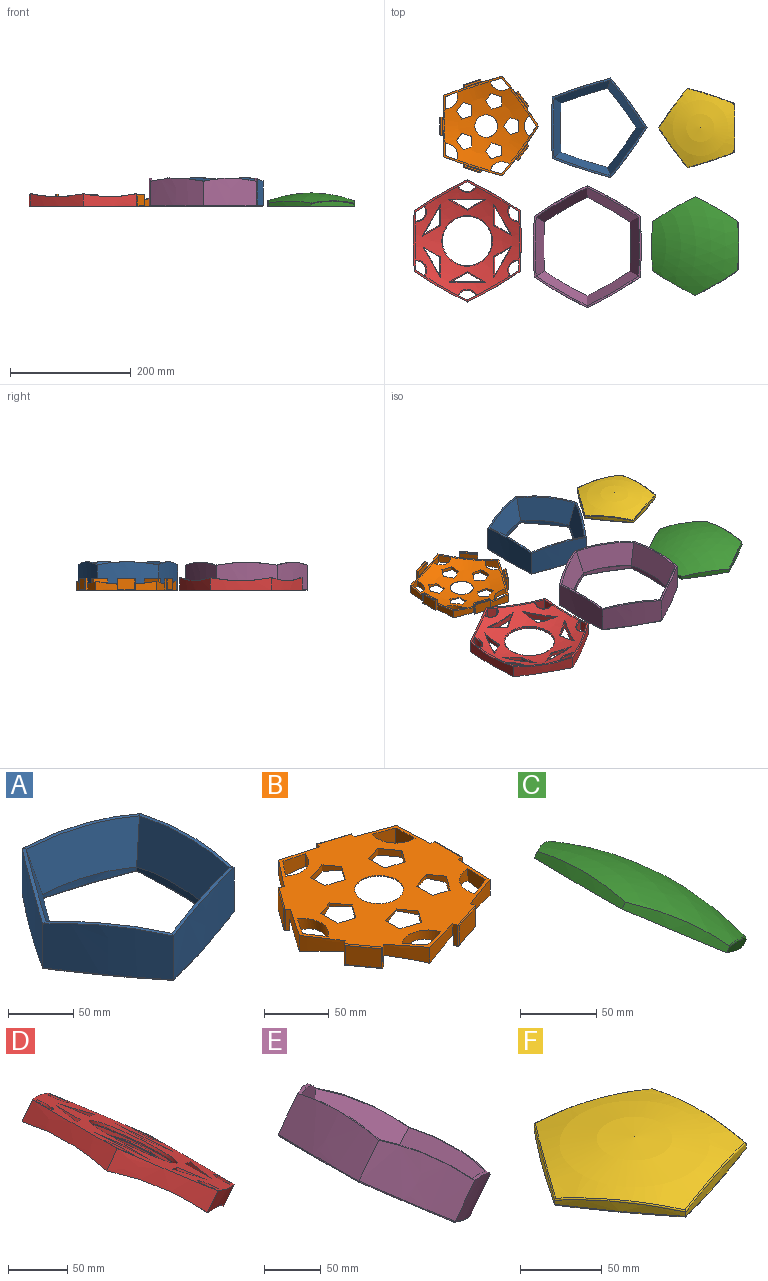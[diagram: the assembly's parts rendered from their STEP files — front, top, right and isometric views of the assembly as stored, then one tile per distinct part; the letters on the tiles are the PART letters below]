
ASSEMBLY  parts=6 mates=5
PART A: 31 faces, bbox 185.7x195.3x47.6 mm
  f0: plane 92.99x43.22mm, normal (-0.3,-0.91,0.28), area 3660.3mm2, adj f1,f2,f9,f15
  f1: plane 97.76x43.22mm, normal (-0.96,0,0.28), area 3660.3mm2, adj f0,f3,f5,f11
  f2: plane 79.14x61.88mm, normal (0.78,-0.56,0.28), area 3660.3mm2, adj f0,f4,f8,f14
  f3: plane 92.99x43.22mm, normal (-0.3,0.91,0.28), area 3660.3mm2, adj f1,f4,f6,f12
  f4: plane 79.14x61.88mm, normal (0.78,0.56,0.28), area 3660.3mm2, adj f2,f3,f7,f13
  f5: extruded ~81.11x7.29mm, area 485.1mm2, adj f1,f6,f9,f28
  f6: extruded ~77.14x25.06mm, area 485.1mm2, adj f3,f5,f7,f26
  f7: extruded ~65.62x47.67mm, area 485.1mm2, adj f4,f6,f8,f27
  f8: extruded ~65.62x47.67mm, area 485.1mm2, adj f2,f7,f9,f29
  f9: extruded ~77.14x25.06mm, area 485.1mm2, adj f0,f5,f8,f30
  f10: plane 162.33x155.86mm, normal (0,0,-1), area 5769.7mm2, adj f21,f22,f23,f24,f25,f26,f27,f28
  f11: bspline ~101.71x5.13mm, area 300.7mm2, adj f1,f12,f15,f18
  f12: bspline ~97.49x34.22mm, area 300.7mm2, adj f3,f11,f13,f19
  f13: bspline ~83.9x62.1mm, area 300.7mm2, adj f4,f12,f14,f20
  f14: bspline ~83.9x62.1mm, area 300.7mm2, adj f2,f13,f15,f16
  f15: bspline ~97.49x34.22mm, area 300.7mm2, adj f0,f11,f14,f17
  f16: extruded ~82.29x59.79mm, area 4192.3mm2, adj f14,f17,f20,f25
  f17: extruded ~96.73x41.19mm, area 4192.3mm2, adj f15,f16,f18,f23
  f18: extruded ~101.71x41.19mm, area 4192.3mm2, adj f11,f17,f19,f21
  f19: extruded ~96.73x41.19mm, area 4192.3mm2, adj f12,f18,f20,f22
  f20: extruded ~82.29x59.79mm, area 4192.3mm2, adj f13,f16,f19,f24
  f21: bspline ~141.48x3.96mm, area 158.8mm2, adj f10,f18,f22,f23
  f22: bspline ~134.78x44.64mm, area 158.8mm2, adj f10,f19,f21,f24
  f23: bspline ~134.78x44.64mm, area 158.8mm2, adj f10,f17,f21,f25
  f24: bspline ~114.98x83.92mm, area 158.8mm2, adj f10,f20,f22,f25
  f25: bspline ~114.98x83.92mm, area 158.8mm2, adj f10,f16,f23,f24
  f26: bspline ~109.03x36.27mm, area 128.5mm2, adj f6,f10,f27,f28
  f27: bspline ~93.07x68mm, area 128.5mm2, adj f7,f10,f26,f29
  f28: bspline ~114.4x3.32mm, area 128.5mm2, adj f5,f10,f26,f30
  f29: bspline ~93.07x68mm, area 128.5mm2, adj f8,f10,f27,f30
  f30: bspline ~109.03x36.27mm, area 128.5mm2, adj f9,f10,f28,f29
PART B: 113 faces, bbox 165.4x167x22.5 mm
  f0: extruded ~50.72x15.01mm, area 441.3mm2, adj f19,f43,f52,f103,f111
  f1: extruded ~48.71x15.01mm, area 441.3mm2, adj f19,f46,f51,f92,f100
  f2: extruded ~41.93x28.58mm, area 441.3mm2, adj f19,f45,f50,f81,f89
  f3: extruded ~40.14x31.04mm, area 441.3mm2, adj f19,f47,f56,f70,f78
  f4: extruded ~47.77x17.12mm, area 441.3mm2, adj f19,f44,f57,f59,f67
  f5: sphere r=242.5mm, area 11570.5mm2, adj f6,f7,f8,f9,f10,f11,f12,f13
  f6: cylinder r=20mm len=31.77mm, axis (0,0,1), area 372.4mm2, adj f5,f19,f40,f53
  f7: cylinder r=20mm len=33.41mm, axis (0,0,1), area 372.4mm2, adj f5,f19,f38,f55
  f8: cylinder r=20mm len=31.77mm, axis (0,0,1), area 372.4mm2, adj f5,f19,f39,f54
  f9: plane 16.51x7.46mm, normal (1,0,0), area 74.6mm2, adj f5,f10,f19,f35
  f10: plane 19.6x7.94mm, normal (0.31,-0.95,0), area 115.8mm2, adj f5,f9,f19,f36
  f11: plane 15.76x7.46mm, normal (0.31,0.95,0), area 74.6mm2, adj f5,f12,f19,f32
  f12: plane 20.52x7.94mm, normal (1,0,0), area 115.8mm2, adj f5,f11,f19,f33
  f13: plane 13.58x10.19mm, normal (-0.81,0.59,0), area 74.6mm2, adj f5,f14,f19,f29
  f14: plane 19.6x7.94mm, normal (0.31,0.95,0), area 115.8mm2, adj f5,f13,f19,f30
  f15: plane 12.88x9.49mm, normal (-0.81,-0.59,0), area 74.6mm2, adj f5,f16,f19,f26
  f16: plane 16.92x12.75mm, normal (-0.81,0.59,0), area 115.8mm2, adj f5,f15,f19,f27
  f17: plane 15.76x7.46mm, normal (0.31,-0.95,0), area 74.6mm2, adj f5,f18,f19,f23
  f18: plane 16.92x12.75mm, normal (-0.81,-0.59,0), area 115.8mm2, adj f5,f17,f19,f24
  f19: plane 164.57x161.91mm, normal (0,0,1), area 13363.7mm2, adj f0,f1,f2,f3,f4,f6,f7,f8
  f20: cylinder r=20mm len=27.05mm, axis (0,0,1), area 372.4mm2, adj f5,f19,f41,f48
  f21: cylinder r=20mm len=27.05mm, axis (0,0,1), area 372.4mm2, adj f5,f19,f42,f49
  f22: cylinder r=18.8mm len=37.59mm, axis (0,0,1), area 86.1mm2, adj f5,f19
  f23: plane 19.95x6.1mm, normal (1,0,0), area 45.3mm2, adj f5,f17,f19,f25
  f24: plane 13.58x10.19mm, normal (-0.81,0.59,0), area 74.6mm2, adj f5,f18,f19,f25
  f25: plane 19.1x7.86mm, normal (0.31,0.95,0), area 45.3mm2, adj f5,f19,f23,f24
  f26: plane 17.53x6.3mm, normal (0.31,-0.95,0), area 45.3mm2, adj f5,f15,f19,f28
  f27: plane 15.76x7.46mm, normal (0.31,0.95,0), area 74.6mm2, adj f5,f16,f19,f28
  f28: plane 19.95x6.1mm, normal (1,0,0), area 45.3mm2, adj f5,f19,f26,f27
  f29: plane 16.61x12.74mm, normal (-0.81,-0.59,0), area 45.3mm2, adj f5,f13,f19,f31
  f30: plane 16.51x7.46mm, normal (1,0,0), area 74.6mm2, adj f5,f14,f19,f31
  f31: plane 19.1x7.86mm, normal (0.31,-0.95,0), area 45.3mm2, adj f5,f19,f29,f30
  f32: plane 16.61x12.74mm, normal (-0.81,0.59,0), area 45.3mm2, adj f5,f11,f19,f34
  f33: plane 15.76x7.46mm, normal (0.31,-0.95,0), area 74.6mm2, adj f5,f12,f19,f34
  f34: plane 16.61x12.74mm, normal (-0.81,-0.59,0), area 45.3mm2, adj f5,f19,f32,f33
  f35: plane 19.1x7.86mm, normal (0.31,0.95,0), area 45.3mm2, adj f5,f9,f19,f37
  f36: plane 13.58x10.19mm, normal (-0.81,-0.59,0), area 74.6mm2, adj f5,f10,f19,f37
  f37: plane 16.61x12.74mm, normal (-0.81,0.59,0), area 45.3mm2, adj f5,f19,f35,f36
  f38: extruded ~16.7x14.63mm, area 261.5mm2, adj f7,f19,f47,f55
  f39: extruded ~15.62x14.63mm, area 261.5mm2, adj f8,f19,f45,f54
  f40: extruded ~19.29x14.63mm, area 261.5mm2, adj f6,f19,f44,f53
  f41: extruded ~19.98x14.63mm, area 261.5mm2, adj f19,f20,f43,f48
  f42: extruded ~18.72x14.63mm, area 261.5mm2, adj f19,f21,f46,f49
  f43: bspline ~101.71x5.12mm, area 300.9mm2, adj f0,f5,f41,f44,f46,f49,f57,f111
  f44: bspline ~97.49x34.22mm, area 300.9mm2, adj f4,f5,f40,f43,f47,f48,f56,f67
  f45: bspline ~83.9x62.1mm, area 300.9mm2, adj f2,f5,f39,f46,f47,f51,f55,f89
  f46: bspline ~97.49x34.22mm, area 300.9mm2, adj f1,f5,f42,f43,f45,f52,f54,f100
  f47: bspline ~83.9x62.1mm, area 300.9mm2, adj f3,f5,f38,f44,f45,f50,f53,f78
  f48: extruded ~18.72x14.63mm, area 261.5mm2, adj f19,f20,f41,f44
  f49: extruded ~19.98x14.63mm, area 261.5mm2, adj f19,f21,f42,f43
  f50: extruded ~41.93x28.58mm, area 441.4mm2, adj f2,f19,f47,f69,f78
  f51: extruded ~40.14x31.05mm, area 441.4mm2, adj f1,f19,f45,f80,f89
  f52: extruded ~47.77x17.12mm, area 441.4mm2, adj f0,f19,f46,f91,f100
  f53: extruded ~15.62x14.63mm, area 261.5mm2, adj f6,f19,f40,f47
  f54: extruded ~19.29x14.63mm, area 261.5mm2, adj f8,f19,f39,f46
  f55: extruded ~16.7x14.63mm, area 261.5mm2, adj f7,f19,f38,f45
  f56: extruded ~48.71x15.01mm, area 441.4mm2, adj f3,f19,f44,f58,f67
  f57: extruded ~50.72x15.01mm, area 441.4mm2, adj f4,f19,f43,f102,f111
  f58: plane 20x3.8mm, normal (-0.95,0.31,0), area 75.7mm2, adj f19,f56,f60,f62,f66,f67,f68
  f59: plane 20x3.8mm, normal (0.95,-0.31,0), area 75.7mm2, adj f4,f19,f60,f65,f66,f67,f68
  f60: plane 29.34x11.74mm, normal (0,0,-1), area 78mm2, adj f58,f59,f63,f68
  f61: plane 26.63x18mm, normal (0.31,0.95,0), area 504mm2, adj f62,f63,f64,f65
  f62: cylinder r=1mm len=20mm, axis (0,0,-1), area 29.8mm2, adj f58,f61,f63,f64
  f63: cylinder r=1mm len=28.84mm, axis (0.95,-0.31,0), area 45.6mm2, adj f60,f61,f62,f65
  f64: cylinder r=1mm len=28.84mm, axis (-0.95,0.31,0), area 45.6mm2, adj f19,f61,f62,f65
  f65: cylinder r=1mm len=20mm, axis (0,0,1), area 29.8mm2, adj f59,f61,f63,f64
  f66: plane 28.53x9.27mm, normal (-0.31,-0.95,0), area 273.5mm2, adj f58,f59,f67,f68
  f67: plane 28.66x9.65mm, normal (0,0,-1), area 9.4mm2, adj f4,f44,f56,f58,f59,f66
  f68: cylinder r=1mm len=28.84mm, axis (0.95,-0.31,0), area 47.1mm2, adj f58,f59,f60,f66
  f69: plane 20x3.24mm, normal (-0.59,-0.81,0), area 75.7mm2, adj f19,f50,f71,f73,f77,f78,f79
  f70: plane 20x3.24mm, normal (0.59,0.81,0), area 75.7mm2, adj f3,f19,f71,f76,f77,f78,f79
  f71: plane 25.8x19.74mm, normal (0,0,-1), area 78mm2, adj f69,f70,f74,f79
  f72: plane 22.65x18mm, normal (-0.81,0.59,0), area 504mm2, adj f73,f74,f75,f76
  f73: cylinder r=1mm len=20mm, axis (0,0,-1), area 29.8mm2, adj f69,f72,f74,f75
  f74: cylinder r=1mm len=24.86mm, axis (0.59,0.81,0), area 45.6mm2, adj f71,f72,f73,f76
  f75: cylinder r=1mm len=24.86mm, axis (-0.59,-0.81,0), area 45.6mm2, adj f19,f72,f73,f76
  f76: cylinder r=1mm len=20mm, axis (0,0,1), area 29.8mm2, adj f70,f72,f74,f75
  f77: plane 24.27x17.63mm, normal (0.81,-0.59,0), area 273.5mm2, adj f69,f70,f78,f79
  f78: plane 24.51x17.96mm, normal (0,0,-1), area 9.4mm2, adj f3,f47,f50,f69,f70,f77
  f79: cylinder r=1mm len=24.86mm, axis (0.59,0.81,0), area 47.1mm2, adj f69,f70,f71,f77
  f80: plane 20x3.24mm, normal (0.59,-0.81,0), area 75.7mm2, adj f19,f51,f82,f84,f88,f89,f90
  f81: plane 20x3.24mm, normal (-0.59,0.81,0), area 75.7mm2, adj f2,f19,f82,f87,f88,f89,f90
  f82: plane 25.8x19.74mm, normal (0,0,-1), area 78mm2, adj f80,f81,f85,f90
  f83: plane 22.65x18mm, normal (-0.81,-0.59,0), area 504mm2, adj f84,f85,f86,f87
  f84: cylinder r=1mm len=20mm, axis (0,0,-1), area 29.8mm2, adj f80,f83,f85,f86
  f85: cylinder r=1mm len=24.86mm, axis (-0.59,0.81,0), area 45.6mm2, adj f82,f83,f84,f87
  f86: cylinder r=1mm len=24.86mm, axis (0.59,-0.81,0), area 45.6mm2, adj f19,f83,f84,f87
  f87: cylinder r=1mm len=20mm, axis (0,0,1), area 29.8mm2, adj f81,f83,f85,f86
  f88: plane 24.27x17.63mm, normal (0.81,0.59,0), area 273.5mm2, adj f80,f81,f89,f90
  f89: plane 24.51x17.96mm, normal (0,0,-1), area 9.4mm2, adj f2,f45,f51,f80,f81,f88
  f90: cylinder r=1mm len=24.86mm, axis (-0.59,0.81,0), area 47.1mm2, adj f80,f81,f82,f88
  f91: plane 20x3.8mm, normal (0.95,0.31,0), area 75.7mm2, adj f19,f52,f93,f95,f99,f100,f101
  f92: plane 20x3.8mm, normal (-0.95,-0.31,0), area 75.7mm2, adj f1,f19,f93,f98,f99,f100,f101
  f93: plane 29.34x11.74mm, normal (0,0,-1), area 78mm2, adj f91,f92,f96,f101
  f94: plane 26.63x18mm, normal (0.31,-0.95,0), area 504mm2, adj f95,f96,f97,f98
  f95: cylinder r=1mm len=20mm, axis (0,0,-1), area 29.8mm2, adj f91,f94,f96,f97
  f96: cylinder r=1mm len=28.84mm, axis (-0.95,-0.31,0), area 45.6mm2, adj f93,f94,f95,f98
  f97: cylinder r=1mm len=28.84mm, axis (0.95,0.31,0), area 45.6mm2, adj f19,f94,f95,f98
  f98: cylinder r=1mm len=20mm, axis (0,0,1), area 29.8mm2, adj f92,f94,f96,f97
  f99: plane 28.53x9.27mm, normal (-0.31,0.95,0), area 273.5mm2, adj f91,f92,f100,f101
  f100: plane 28.66x9.65mm, normal (0,0,-1), area 9.4mm2, adj f1,f46,f52,f91,f92,f99
  f101: cylinder r=1mm len=28.84mm, axis (-0.95,-0.31,0), area 47.1mm2, adj f91,f92,f93,f99
  f102: plane 20x4mm, normal (0,1,0), area 75.7mm2, adj f19,f57,f104,f106,f110,f111,f112
  f103: plane 20x4mm, normal (0,-1,0), area 75.7mm2, adj f0,f19,f104,f109,f110,f111,f112
  f104: plane 30x2.6mm, normal (0,0,-1), area 78mm2, adj f102,f103,f107,f112
  f105: plane 28x18mm, normal (1,0,0), area 504mm2, adj f106,f107,f108,f109
  f106: cylinder r=1mm len=20mm, axis (0,0,-1), area 29.8mm2, adj f102,f105,f107,f108
  f107: cylinder r=1mm len=30mm, axis (0,-1,0), area 45.6mm2, adj f104,f105,f106,f109
  f108: cylinder r=1mm len=30mm, axis (0,1,0), area 45.6mm2, adj f19,f105,f106,f109
  f109: cylinder r=1mm len=20mm, axis (0,0,1), area 29.8mm2, adj f103,f105,f107,f108
  f110: plane 30x9.12mm, normal (-1,0,0), area 273.5mm2, adj f102,f103,f111,f112
  f111: plane 30x0.4mm, normal (0,0,-1), area 9.4mm2, adj f0,f43,f57,f102,f103,f110
  f112: cylinder r=1mm len=30mm, axis (0,-1,0), area 47.1mm2, adj f102,f103,f104,f110
PART C: 27 faces, bbox 126.4x203x94.5 mm
  f0: plane 29.86x26.12mm, normal (0.4,0.87,-0.3), area 345.6mm2, adj f1,f2,f18,f26
  f1: cylinder r=15.23mm len=15.44mm, axis (-0.61,0,-0.79), area 161.9mm2, adj f0,f3,f18,f26
  f2: cylinder r=50mm len=50mm, axis (-0.61,0,-0.79), area 523.6mm2, adj f0,f3,f18,f26
  f3: plane 29.86x26.12mm, normal (0.4,-0.87,-0.3), area 345.6mm2, adj f1,f2,f18,f26
  f4: cylinder r=50mm len=40.48mm, axis (-0.61,0,-0.79), area 523.6mm2, adj f5,f6,f18,f25
  f5: plane 34.77x7.95mm, normal (-0.79,0,0.61), area 347.7mm2, adj f4,f7,f18,f25
  f6: plane 30.14x26.33mm, normal (0.4,-0.87,-0.3), area 349.7mm2, adj f4,f7,f18,f25
  f7: cylinder r=15.23mm len=16.41mm, axis (-0.61,0,-0.79), area 158.4mm2, adj f5,f6,f18,f25
  f8: plane 34.77x7.95mm, normal (-0.79,0,0.61), area 347.7mm2, adj f9,f10,f18,f24
  f9: cylinder r=15.23mm len=16.41mm, axis (-0.61,0,-0.79), area 158.4mm2, adj f8,f11,f18,f24
  f10: cylinder r=50mm len=40.48mm, axis (-0.61,0,-0.79), area 523.6mm2, adj f8,f11,f18,f24
  f11: plane 30.14x26.33mm, normal (0.4,0.87,-0.3), area 349.7mm2, adj f9,f10,f18,f24
  f12: cylinder r=10mm len=21.96mm, axis (-0.61,0,-0.79), area 628.3mm2, adj f18,f23
  f13: sphere r=202.5mm, area 18663.9mm2, adj f16,f17,f19,f20,f21,f22
  f14: extruded ~61.02x49.32mm, area 561.6mm2, adj f15,f17,f18,f21
  f15: extruded ~81.46x7.4mm, area 561.6mm2, adj f14,f16,f18,f22
  f16: extruded ~61.44x49.87mm, area 617.9mm2, adj f13,f15,f18,f19,f22
  f17: extruded ~61.44x49.87mm, area 617.9mm2, adj f13,f14,f18,f20,f21
  f18: plane 162.92x114.47mm, normal (-0.61,0,-0.79), area 13845.5mm2, adj f0,f1,f2,f3,f4,f5,f6,f7
  f19: extruded ~61.44x49.87mm, area 618.1mm2, adj f13,f16,f18,f20
  f20: extruded ~81.46x7.94mm, area 618.1mm2, adj f13,f17,f18,f19
  f21: bspline ~62.43x48.26mm, area 99.2mm2, adj f13,f14,f17,f22
  f22: bspline ~91.5x4.94mm, area 99.2mm2, adj f13,f15,f16,f21
  f23: plane 20x15.89mm, normal (-0.61,0,-0.79), area 314.2mm2, adj f12
  f24: plane 42.48x34.41mm, normal (-0.61,0,-0.79), area 1189.3mm2, adj f8,f9,f10,f11
  f25: plane 42.48x34.41mm, normal (-0.61,0,-0.79), area 1189.3mm2, adj f4,f5,f6,f7
  f26: plane 50x29.11mm, normal (-0.61,0,-0.79), area 1183.9mm2, adj f0,f1,f2,f3
PART D: 75 faces, bbox 163.4x243.7x126.1 mm
  f0: sphere r=242.5mm, area 16081.2mm2, adj f23,f33,f34,f35,f36,f37,f38,f51
  f1: cylinder r=16.14mm len=25.05mm, axis (0.61,0,0.79), area 598.9mm2, adj f6,f29,f42,f73
  f2: cylinder r=16.14mm len=25.05mm, axis (0.61,0,0.79), area 598.9mm2, adj f6,f28,f41,f72
  f3: cylinder r=16.14mm len=33.12mm, axis (0.61,0,0.79), area 598.9mm2, adj f6,f27,f40,f71
  f4: cylinder r=16.14mm len=25.05mm, axis (0.61,0,0.79), area 598.9mm2, adj f6,f30,f39,f70
  f5: cylinder r=16.14mm len=25.05mm, axis (0.61,0,0.79), area 598.9mm2, adj f6,f32,f44,f69
  f6: plane 201.9x141.94mm, normal (0.61,0,0.79), area 17762.9mm2, adj f1,f2,f3,f4,f5,f7,f8,f9
  f7: cylinder r=16.14mm len=33.12mm, axis (0.61,0,0.79), area 598.9mm2, adj f6,f31,f43,f51
  f8: plane 24.04x23.88mm, normal (-0.4,-0.87,0.3), area 211mm2, adj f6,f9,f10,f53
  f9: plane 48.87x40.81mm, normal (0,1,0), area 500mm2, adj f6,f8,f10,f52,f53,f54
  f10: plane 27.17x19.73mm, normal (0.4,-0.87,-0.3), area 211mm2, adj f6,f8,f9,f52
  f11: plane 30.73x7.88mm, normal (-0.79,0,0.61), area 211mm2, adj f6,f12,f13,f56
  f12: plane 46.54x27.64mm, normal (0.69,0.5,-0.53), area 500mm2, adj f6,f11,f13,f55,f56,f57
  f13: plane 27.17x19.73mm, normal (-0.4,-0.87,0.3), area 211mm2, adj f6,f11,f12,f55
  f14: plane 27.17x19.73mm, normal (-0.4,0.87,0.3), area 211mm2, adj f6,f15,f16,f59
  f15: plane 46.54x27.64mm, normal (0.69,-0.5,-0.53), area 500mm2, adj f6,f14,f16,f58,f59,f60
  f16: plane 30.73x7.88mm, normal (-0.79,0,0.61), area 211mm2, adj f6,f14,f15,f58
  f17: plane 27.17x19.73mm, normal (0.4,0.87,-0.3), area 211mm2, adj f6,f18,f19,f62
  f18: plane 48.87x40.81mm, normal (0,-1,0), area 500mm2, adj f6,f17,f19,f61,f62,f63
  f19: plane 24.04x23.88mm, normal (-0.4,0.87,0.3), area 211mm2, adj f6,f17,f18,f61
  f20: plane 30.73x7.88mm, normal (0.79,0,-0.61), area 211mm2, adj f6,f21,f22,f65
  f21: plane 46.54x27.64mm, normal (-0.69,-0.5,0.53), area 500mm2, adj f6,f20,f22,f64,f65,f66
  f22: plane 24.04x23.88mm, normal (0.4,0.87,-0.3), area 211mm2, adj f6,f20,f21,f64
  f23: plane 27.2x26.6mm, normal (0.4,-0.87,-0.3), area 249.2mm2, adj f0,f6,f24,f25,f67,f68
  f24: plane 46.35x27.64mm, normal (-0.69,0.5,0.53), area 499.9mm2, adj f6,f23,f25,f67,f68
  f25: plane 30.73x7.88mm, normal (0.79,0,-0.61), area 211mm2, adj f6,f23,f24,f67
  f26: cylinder r=40.98mm len=81.96mm, axis (0.61,0,0.79), area 681.3mm2, adj f6,f74
  f27: extruded ~25.66x24.71mm, area 311mm2, adj f3,f6,f37,f40,f71
  f28: extruded ~25.03x23.89mm, area 311mm2, adj f2,f6,f38,f41,f72
  f29: extruded ~17.21x16.92mm, area 311mm2, adj f1,f6,f33,f42,f73
  f30: extruded ~17.22x16.92mm, area 311mm2, adj f4,f6,f36,f39,f70
  f31: extruded ~25.66x24.71mm, area 311mm2, adj f6,f7,f34,f43,f51
  f32: extruded ~25.03x23.89mm, area 311mm2, adj f5,f6,f35,f44,f69
  f33: bspline ~100.97x6.6mm, area 299.9mm2, adj f0,f29,f34,f38,f41,f47
  f34: bspline ~71.27x54.2mm, area 299.7mm2, adj f0,f31,f33,f35,f42,f48
  f35: bspline ~70.49x53.85mm, area 299.7mm2, adj f0,f32,f34,f36,f43,f49
  f36: bspline ~100.93x6.85mm, area 299.7mm2, adj f0,f30,f35,f37,f44,f50
  f37: bspline ~71.33x54.25mm, area 299.7mm2, adj f0,f27,f36,f38,f39,f45
  f38: bspline ~69.63x53.06mm, area 299.9mm2, adj f0,f28,f33,f37,f40,f46
  f39: extruded ~25.03x23.89mm, area 311mm2, adj f4,f6,f30,f37,f70
  f40: extruded ~25.66x24.71mm, area 311mm2, adj f3,f6,f27,f38,f71
  f41: extruded ~17.22x16.92mm, area 311mm2, adj f2,f6,f28,f33,f72
  f42: extruded ~25.03x23.89mm, area 311mm2, adj f1,f6,f29,f34,f73
  f43: extruded ~25.66x24.71mm, area 311mm2, adj f6,f7,f31,f35,f51
  f44: extruded ~17.22x16.92mm, area 311mm2, adj f5,f6,f32,f36,f69
  f45: extruded ~82.08x69.58mm, area 2099.9mm2, adj f6,f37,f46,f50
  f46: extruded ~82.08x69.58mm, area 2100mm2, adj f6,f38,f45,f47
  f47: extruded ~100.93x17.66mm, area 2100mm2, adj f6,f33,f46,f48
  f48: extruded ~82.08x69.58mm, area 2099.9mm2, adj f6,f34,f47,f49
  f49: extruded ~82.08x69.58mm, area 2099.8mm2, adj f6,f35,f48,f50
  f50: extruded ~100.93x17.66mm, area 2099.8mm2, adj f6,f36,f45,f49
  f51: bspline ~25.55x19.73mm, area 68.9mm2, adj f0,f7,f31,f43
  f52: torus R=239.43mm, axis (-0.4,0.87,0.3), area 57.7mm2, adj f0,f9,f10,f53,f54
  f53: torus R=239.43mm, axis (0.4,0.87,-0.3), area 57.7mm2, adj f0,f8,f9,f52,f54
  f54: torus R=233.61mm, axis (0,1,0), area 73.5mm2, adj f0,f9,f52,f53
  f55: torus R=239.43mm, axis (0.4,0.87,-0.3), area 57.7mm2, adj f0,f12,f13,f56,f57
  f56: torus R=239.43mm, axis (0.79,0,-0.61), area 57.7mm2, adj f0,f11,f12,f55,f57
  f57: torus R=233.61mm, axis (0.69,0.5,-0.53), area 73.5mm2, adj f0,f12,f55,f56
  f58: torus R=239.43mm, axis (0.79,0,-0.61), area 57.7mm2, adj f0,f15,f16,f59,f60
  f59: torus R=239.43mm, axis (0.4,-0.87,-0.3), area 57.7mm2, adj f0,f14,f15,f58,f60
  f60: torus R=233.61mm, axis (0.69,-0.5,-0.53), area 73.5mm2, adj f0,f15,f58,f59
  f61: torus R=239.43mm, axis (0.4,-0.87,-0.3), area 57.7mm2, adj f0,f18,f19,f62,f63
  f62: torus R=239.43mm, axis (-0.4,-0.87,0.3), area 57.7mm2, adj f0,f17,f18,f61,f63
  f63: torus R=233.61mm, axis (0,-1,0), area 73.5mm2, adj f0,f18,f61,f62
  f64: torus R=239.43mm, axis (-0.4,-0.87,0.3), area 57.7mm2, adj f0,f21,f22,f65,f66
  f65: torus R=239.43mm, axis (-0.79,0,0.61), area 57.7mm2, adj f0,f20,f21,f64,f66
  f66: torus R=233.61mm, axis (-0.69,-0.5,0.53), area 73.5mm2, adj f0,f21,f64,f65
  f67: torus R=239.43mm, axis (-0.79,0,0.61), area 56.6mm2, adj f0,f23,f24,f25,f68
  f68: torus R=233.61mm, axis (-0.69,0.5,0.53), area 71.8mm2, adj f0,f23,f24,f67
  f69: bspline ~28.14x14.95mm, area 68.9mm2, adj f0,f5,f32,f44
  f70: bspline ~27.82x15.46mm, area 68.9mm2, adj f0,f4,f30,f39
  f71: bspline ~25.35x19.96mm, area 68.9mm2, adj f0,f3,f27,f40
  f72: bspline ~28.13x17.56mm, area 68.9mm2, adj f0,f2,f28,f41
  f73: bspline ~27.82x18.08mm, area 69mm2, adj f0,f1,f29,f42
  f74: torus R=41.98mm, axis (-0.61,0,-0.79), area 362.4mm2, adj f0,f26
PART E: 41 faces, bbox 174.5x209.6x148.6 mm
  f0: plane 97.83x37.34mm, normal (-0.53,0,0.85), area 3560.4mm2, adj f1,f2,f11,f15,f25
  f1: plane 89.22x71.77mm, normal (-0.15,-0.81,0.57), area 3545.1mm2, adj f0,f4,f14,f25
  f2: plane 89.34x71.87mm, normal (-0.15,0.81,0.57), area 3560.4mm2, adj f0,f3,f6,f16,f28
  f3: plane 80.1x78.31mm, normal (0.59,0.81,0), area 3545.1mm2, adj f2,f5,f17,f28
  f4: plane 80.1x78.31mm, normal (0.59,-0.81,0), area 3545.1mm2, adj f1,f5,f13,f26
  f5: plane 97.67x41.74mm, normal (0.96,0,-0.28), area 3544.8mm2, adj f3,f4,f18,f27
  f6: extruded ~61.32x49.62mm, area 580.4mm2, adj f2,f7,f11,f28,f38
  f7: extruded ~61.2x49.47mm, area 565.1mm2, adj f6,f8,f28,f36
  f8: extruded ~81.68x7.42mm, area 565.1mm2, adj f7,f9,f27,f35
  f9: extruded ~61.2x49.47mm, area 565.1mm2, adj f8,f10,f26,f37
  f10: extruded ~61.2x49.47mm, area 565.1mm2, adj f9,f11,f25,f39
  f11: extruded ~81.7x7.57mm, area 580.4mm2, adj f0,f6,f10,f25,f40
  f12: plane 199.66x140.33mm, normal (-0.61,0,-0.79), area 8313.7mm2, adj f29,f30,f31,f32,f33,f34,f35,f36
  f13: bspline ~70.49x53.85mm, area 299.7mm2, adj f4,f14,f18,f21
  f14: bspline ~70.49x53.85mm, area 299.7mm2, adj f1,f13,f15,f22
  f15: bspline ~100.93x6.86mm, area 299.7mm2, adj f0,f14,f16,f23
  f16: bspline ~70.49x53.85mm, area 299.7mm2, adj f2,f15,f17,f24
  f17: bspline ~70.49x53.85mm, area 299.7mm2, adj f3,f16,f18,f19
  f18: bspline ~100.93x6.87mm, area 299.9mm2, adj f5,f13,f17,f20
  f19: extruded ~93.94x85.11mm, area 4073.6mm2, adj f17,f20,f24,f34
  f20: extruded ~100.93x33.19mm, area 4073.6mm2, adj f18,f19,f21,f32
  f21: extruded ~93.94x85.11mm, area 4073.6mm2, adj f13,f20,f22,f30
  f22: extruded ~93.94x85.11mm, area 4073.6mm2, adj f14,f21,f23,f29
  f23: extruded ~100.93x33.19mm, area 4073.6mm2, adj f15,f22,f24,f31
  f24: extruded ~93.94x85.11mm, area 4073.6mm2, adj f16,f19,f23,f33
  f25: bspline ~62.4x47.8mm, area 30.2mm2, adj f0,f1,f10,f11,f26
  f26: bspline ~62.36x47.84mm, area 30.2mm2, adj f4,f9,f25,f27
  f27: bspline ~102.69x8.25mm, area 30.2mm2, adj f5,f8,f26,f28
  f28: bspline ~62.4x47.77mm, area 30.2mm2, adj f2,f3,f6,f7,f27
  f29: bspline ~82.45x63.06mm, area 157.9mm2, adj f12,f22,f30,f31
  f30: bspline ~82.12x63.32mm, area 157.9mm2, adj f12,f21,f29,f32
  f31: bspline ~118.44x3.45mm, area 157.9mm2, adj f12,f23,f29,f33
  f32: bspline ~118.44x2.97mm, area 157.9mm2, adj f12,f20,f30,f34
  f33: bspline ~82.45x63.06mm, area 157.9mm2, adj f12,f24,f31,f34
  f34: bspline ~82.12x63.32mm, area 157.9mm2, adj f12,f19,f32,f33
  f35: bspline ~97.98x3.08mm, area 129.3mm2, adj f8,f12,f36,f37
  f36: bspline ~68.37x52.21mm, area 129.3mm2, adj f7,f12,f35,f38
  f37: bspline ~68.37x52.21mm, area 129.3mm2, adj f9,f12,f35,f39
  f38: bspline ~67.91x52.56mm, area 129.3mm2, adj f6,f12,f36,f40
  f39: bspline ~67.91x52.56mm, area 129.3mm2, adj f10,f12,f37,f40
  f40: bspline ~97.98x2.69mm, area 129.3mm2, adj f11,f12,f38,f39
PART F: 17 faces, bbox 148.4x156.1x17.2 mm
  f0: sphere r=202.5mm, area 14445.2mm2, adj f7,f8,f9,f10,f11
  f1: extruded ~77.4x25.15mm, area 479.8mm2, adj f2,f5,f10,f13
  f2: extruded ~81.38x7.21mm, area 479.8mm2, adj f1,f3,f8,f12
  f3: extruded ~77.4x25.15mm, area 479.8mm2, adj f2,f4,f7,f14
  f4: extruded ~65.84x47.84mm, area 479.8mm2, adj f3,f5,f9,f16
  f5: extruded ~65.84x47.84mm, area 479.8mm2, adj f1,f4,f11,f15
  f6: plane 129.43x124.23mm, normal (0,0,-1), area 11310.2mm2, adj f12,f13,f14,f15,f16
  f7: bspline ~86.04x28.58mm, area 104.8mm2, adj f0,f3,f8,f9
  f8: bspline ~92.26x6.23mm, area 104.8mm2, adj f0,f2,f7,f10
  f9: bspline ~73.42x53.63mm, area 104.8mm2, adj f0,f4,f7,f11
  f10: bspline ~86.05x28.55mm, area 104.8mm2, adj f0,f1,f8,f11
  f11: bspline ~73.43x53.61mm, area 104.8mm2, adj f0,f5,f9,f10
  f12: bspline ~105.46x2.97mm, area 126.8mm2, adj f2,f6,f13,f14
  f13: bspline ~107.82x35.88mm, area 126.8mm2, adj f1,f6,f12,f15
  f14: bspline ~107.82x35.88mm, area 126.8mm2, adj f3,f6,f12,f16
  f15: bspline ~92.04x67.25mm, area 126.8mm2, adj f5,f6,f13,f16
  f16: bspline ~92.04x67.25mm, area 126.8mm2, adj f4,f6,f14,f15
PLACE A rot(axis=(0,0,-1),180deg) t=(-249.23,352.94,116.2)mm
PLACE B rot(axis=(0,-1,0),180deg) t=(-428.49,355.74,544)mm
PLACE C rot(axis=(0,-1,0),37.4deg) t=(-82.89,157.38,121.11)mm
PLACE D rot(axis=(0,1,0),142.6deg) t=(-459.96,165.92,544)mm
PLACE E rot(axis=(0,-1,0),37.4deg) t=(-261.45,156.52,121.11)mm
PLACE F rot(axis=(-0.29,0.82,-0.5),0deg) t=(-74.45,352.65,116.2)mm
MATE planar F.f6 <-> B.f19  axis (0,0,-1) through (-74.45,352.65,301.5)mm
MATE planar C.f18 <-> E.f12  axis (0,0,-1) through (-54.55,173.74,301.5)mm
MATE planar C.f18 <-> F.f6  axis (0,0,-1) through (-54.55,173.74,301.5)mm
MATE planar A.f10 <-> F.f6  axis (0,0,-1) through (-249.23,352.94,301.5)mm
MATE planar C.f18 <-> D.f6  axis (0,0,-1) through (-54.55,173.74,301.5)mm
